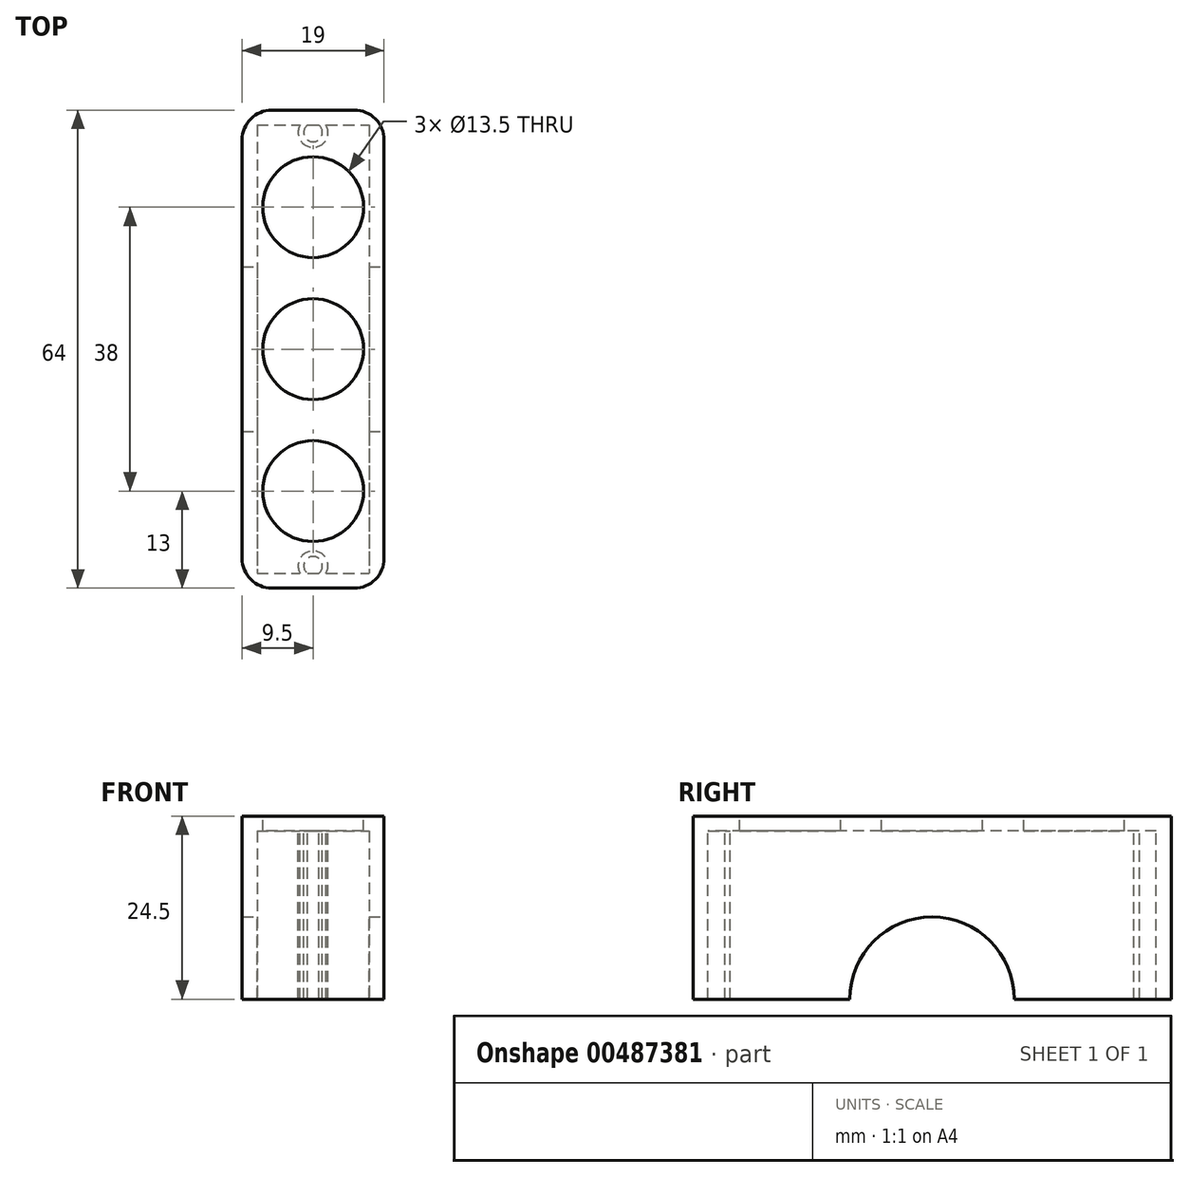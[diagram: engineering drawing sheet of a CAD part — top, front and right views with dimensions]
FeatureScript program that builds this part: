
annotation { "Feature Type Name" : "Feature", "Feature Type Description" : "" }
export const myFeature = defineFeature(function(context is Context, id is Id, definition is map)
    precondition{}
    {
        {
            var Q0;
            Q0=qCreatedBy(makeId("Top.planeOp"),FACE);
            var sketch = newSketch(context, id + "F0", { "sketchPlane" : qUnion([Q0])});
            skLineSegment(sketch, "E0.bottom", {"start": v(-19, 64) * mm, "end": v(0, 64) * mm});
            skLineSegment(sketch, "E0.top", {"start": v(-19, 0) * mm, "end": v(0, 0) * mm});
            skLineSegment(sketch, "E0.left", {"start": v(-19, 64) * mm, "end": v(-19, 0) * mm});
            skLineSegment(sketch, "E0.right", {"start": v(0, 64) * mm, "end": v(0, 0) * mm});
            skSolve(sketch);
        }
        {
            var Q0;
            Q0=qSketchRegion(id+"F0",true);
            extrude(context, id + "F1", {"entities" : qUnion([Q0]), "depth" : 24.5 * mm, "offsetDistance" : 25 * mm});
        }
        {
            var Q0;
            Q0=makeQuery(id+"F1.opExtrude","SWEPT_FACE",FACE,{"disambiguationData":[OSD([sQuery(id+"F0.wireOp",EDGE,"E0.right")])]});
            var sketch = newSketch(context, id + "F2", { "sketchPlane" : qUnion([Q0])});
            skArc(sketch, "E1", {"start": v(43, 0) * mm, "mid": v(32, 11) * mm, "end": v(21, 0) * mm});
            skLineSegment(sketch, "E2", {"start": v(21, 0) * mm, "end": v(43, 0) * mm});
            skSolve(sketch);
        }
        {
            var Q0;
            Q0=qSketchRegion(id+"F2",true);
            extrude(context, id + "F3", {"entities" : qUnion([Q0]), "operationType" : NewBodyOperationType.REMOVE, "oppositeDirection" : true, "depth" : 25 * mm});
        }
        {
            var Q0;
            Q0=makeQuery(id+"F3.boolean.opBoolean","COPY",FACE,{"derivedFrom":makeQuery(id+"F3.opExtrude","SWEPT_FACE",FACE,{"disambiguationData":[OSD([sQuery(id+"F2.wireOp",EDGE,"E1")])]})});
            var Q1;
            {var subQ0=sQuery(id+"F0.wireOp",EDGE,"E0.top");var subQ1=sQuery(id+"F0.wireOp",EDGE,"E0.left");var subQ2=sQuery(id+"F0.wireOp",EDGE,"E0.right");Q1=makeQuery(id+"F3.boolean.opBoolean","SPLIT",FACE,{"disambiguationData":[TD([makeQuery(id+"F1.opExtrude","SWEPT_FACE",FACE,{"disambiguationData":[OSD([subQ0])]})])],"derivedFrom":makeQuery(id+"F1.opExtrude","CAP_FACE",FACE,{"disambiguationData":[OSD([sQuery(id+"F0.wireOp",EDGE,"E0.bottom"),subQ0,subQ1,subQ2])],"isStart":true})});}
            var Q2;
            {var subQ0=sQuery(id+"F0.wireOp",EDGE,"E0.bottom");var subQ1=sQuery(id+"F0.wireOp",EDGE,"E0.right");var subQ2=sQuery(id+"F0.wireOp",EDGE,"E0.left");Q2=makeQuery(id+"F3.boolean.opBoolean","SPLIT",FACE,{"disambiguationData":[TD([makeQuery(id+"F1.opExtrude","SWEPT_FACE",FACE,{"disambiguationData":[OSD([subQ0])]})])],"derivedFrom":makeQuery(id+"F1.opExtrude","CAP_FACE",FACE,{"disambiguationData":[OSD([subQ0,sQuery(id+"F0.wireOp",EDGE,"E0.top"),subQ2,subQ1])],"isStart":true})});}
            shell(context, id + "F4", {"entities" : qUnion([Q0, Q1, Q2]), "thickness" : 2 * mm});
        }
        {
            var Q0;
            Q0=makeQuery(id+"F1.opExtrude","SWEPT_EDGE",EDGE,{"disambiguationData":[OSD([sQuery(id+"F0.wireOp",EDGE,"E0.top"),sQuery(id+"F0.wireOp",EDGE,"E0.right")])]});
            var Q1;
            Q1=makeQuery(id+"F1.opExtrude","SWEPT_EDGE",EDGE,{"disambiguationData":[OSD([sQuery(id+"F0.wireOp",EDGE,"E0.bottom"),sQuery(id+"F0.wireOp",EDGE,"E0.right")])]});
            var Q2;
            Q2=makeQuery(id+"F1.opExtrude","SWEPT_EDGE",EDGE,{"disambiguationData":[OSD([sQuery(id+"F0.wireOp",EDGE,"E0.bottom"),sQuery(id+"F0.wireOp",EDGE,"E0.left")])]});
            var Q3;
            Q3=makeQuery(id+"F1.opExtrude","SWEPT_EDGE",EDGE,{"disambiguationData":[OSD([sQuery(id+"F0.wireOp",EDGE,"E0.top"),sQuery(id+"F0.wireOp",EDGE,"E0.left")])]});
            fillet(context, id + "F5", {"entities" : qUnion([Q0, Q1, Q2, Q3]), "radius" : 4 * mm, "tangentPropagation" : true, "allowEdgeOverflow" : false});
        }
        {
            var Q0;
            Q0=makeQuery(id+"F1.opExtrude","CAP_FACE",FACE,{"disambiguationData":[OSD([sQuery(id+"F0.wireOp",EDGE,"E0.bottom"),sQuery(id+"F0.wireOp",EDGE,"E0.top"),sQuery(id+"F0.wireOp",EDGE,"E0.left"),sQuery(id+"F0.wireOp",EDGE,"E0.right")])],"isStart":false});
            var sketch = newSketch(context, id + "F6", { "sketchPlane" : qUnion([Q0])});
            skCircle(sketch, "E3", {"center": v(-9.5, 32) * mm, "radius": 6.75 * mm});
            skPoint(sketch, "E3.centerSnap0", {"position": v(-19, 32) * mm});
            skSolve(sketch);
        }
        {
            var Q0;
            Q0=qSketchRegion(id+"F6",true);
            extrude(context, id + "F7", {"entities" : qUnion([Q0]), "operationType" : NewBodyOperationType.REMOVE, "oppositeDirection" : true, "offsetDistance" : 25 * mm, "depth" : 25 * mm});
        }
        {
            var Q0;
            Q0=makeQuery(id+"F4.opShell","OFFSET_FACE",FACE,{"disambiguationData":[OSD([sQuery(id+"F0.wireOp",EDGE,"E0.bottom"),sQuery(id+"F0.wireOp",EDGE,"E0.top"),sQuery(id+"F0.wireOp",EDGE,"E0.left"),sQuery(id+"F0.wireOp",EDGE,"E0.right")])]});
            var sketch = newSketch(context, id + "F8", { "sketchPlane" : qUnion([Q0])});
            skCircle(sketch, "E4", {"center": v(-9.5, -3) * mm, "radius": 2 * mm});
            skCircle(sketch, "E5", {"center": v(-9.5, -3) * mm, "radius": 1.25 * mm});
            skLineSegment(sketch, "E6", {"start": v(-17, -32) * mm, "end": v(-2, -32) * mm, "construction": true});
            skCircle(sketch, "E7.MirrorC", {"center": v(-9.5, -61) * mm, "radius": 2 * mm});
            skCircle(sketch, "E8.MirrorC", {"center": v(-9.5, -61) * mm, "radius": 1.25 * mm});
            skSolve(sketch);
        }
        {
            var Q0;
            Q0=qSketchRegion(id+"F8",true);
            extrude(context, id + "F9", {"entities" : qUnion([Q0]), "operationType" : NewBodyOperationType.ADD, "depth" : 22.5 * mm, "offsetDistance" : 25 * mm});
        }
        {
            var Q0;
            {var subQ0=sQuery(id+"F0.wireOp",EDGE,"E0.left");var subQ1=sQuery(id+"F0.wireOp",EDGE,"E0.bottom");var subQ2=sQuery(id+"F0.wireOp",EDGE,"E0.right");Q0=makeQuery(id+"FS9lYY6Vs6I1Vlx_1.boolean.opBoolean","SPLIT",FACE,{"disambiguationData":[TD([makeQuery(id+"F1.opExtrude","SWEPT_FACE",FACE,{"disambiguationData":[OSD([subQ1])]})])],"derivedFrom":makeQuery(id+"F1.opExtrude","CAP_FACE",FACE,{"disambiguationData":[OSD([subQ1,sQuery(id+"F0.wireOp",EDGE,"E0.top"),subQ0,subQ2])],"isStart":false})});}
            var sketch = newSketch(context, id + "F10", { "sketchPlane" : qUnion([Q0])});
            skCircle(sketch, "E9", {"center": v(-9.5, 51) * mm, "radius": 6.75 * mm});
            skLineSegment(sketch, "E10", {"start": v(-19, 32) * mm, "end": v(0, 32) * mm, "construction": true});
            skCircle(sketch, "E11.MirrorC", {"center": v(-9.5, 13) * mm, "radius": 6.75 * mm});
            skSolve(sketch);
        }
        {
            var Q0;
            Q0=qSketchRegion(id+"F10",true);
            extrude(context, id + "F11", {"entities" : qUnion([Q0]), "operationType" : NewBodyOperationType.REMOVE, "oppositeDirection" : true, "offsetDistance" : 25 * mm, "depth" : 25 * mm});
        }
    });
